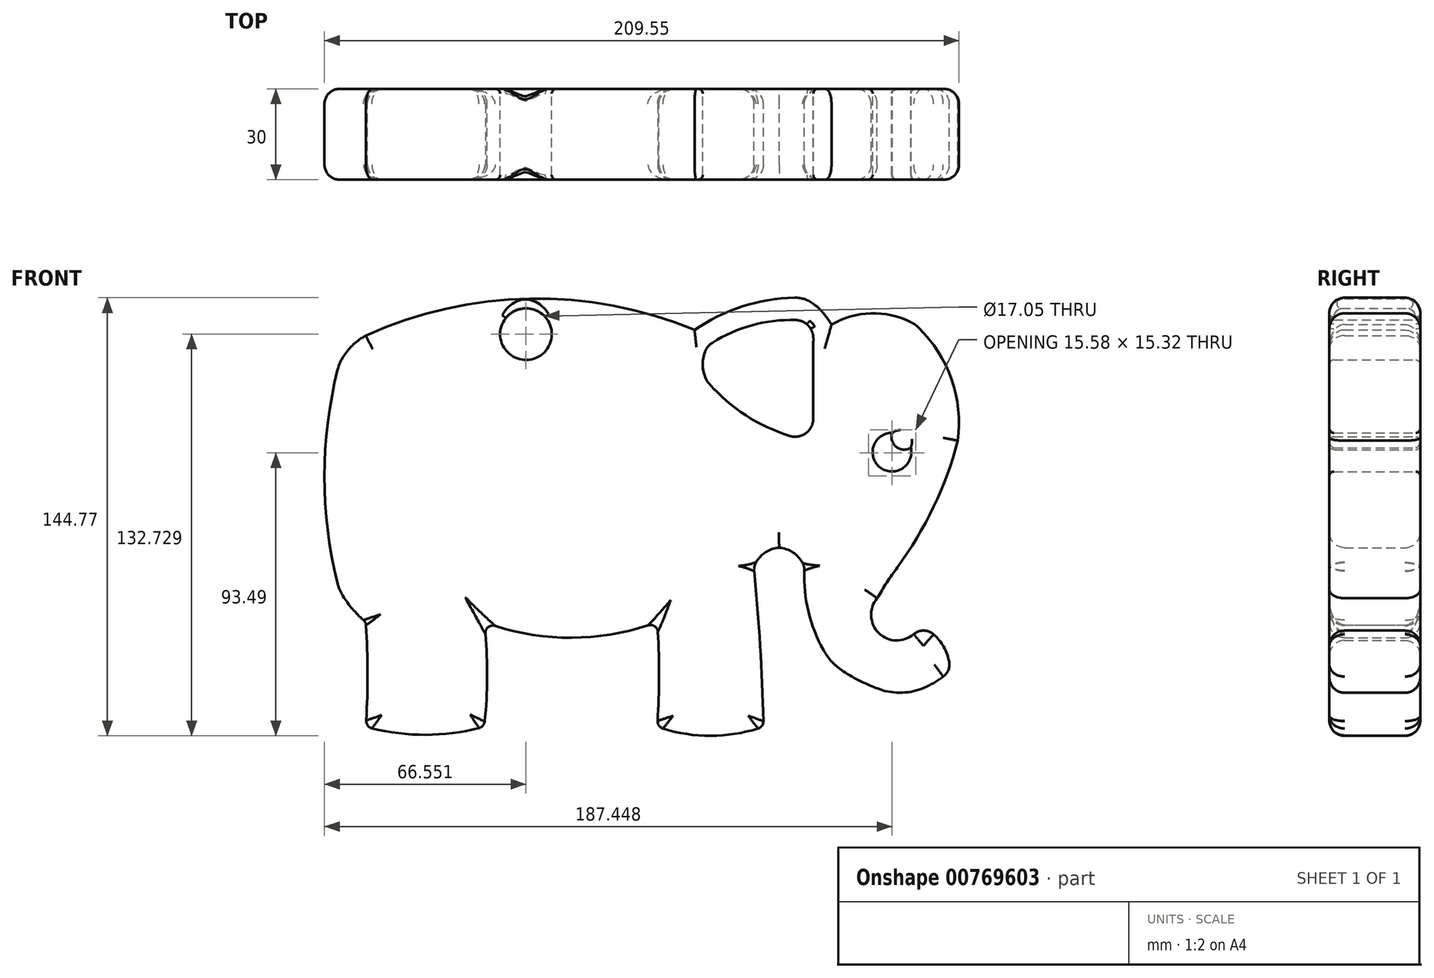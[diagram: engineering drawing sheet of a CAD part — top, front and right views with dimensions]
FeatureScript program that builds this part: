
annotation { "Feature Type Name" : "Feature", "Feature Type Description" : "" }
export const myFeature = defineFeature(function(context is Context, id is Id, definition is map)
    precondition{}
    {
        {
            var Q0;
            Q0=qCreatedBy(makeId("Front.planeOp"),FACE);
            var sketch = newSketch(context, id + "F0", { "sketchPlane" : qUnion([Q0])});
            skArc(sketch, "E0", {"start": v(19.89, -18.97) * mm, "mid": v(21.78, -31.57) * mm, "end": v(34.05, -28.13) * mm});
            skArc(sketch, "E1", {"start": v(27.2, -50.9) * mm, "mid": v(36.15, -48.2) * mm, "end": v(43.95, -43.06) * mm});
            skArc(sketch, "E2", {"start": v(4.8, -40.36) * mm, "mid": v(15.42, -46.87) * mm, "end": v(27.2, -50.9) * mm});
            skArc(sketch, "E3", {"start": v(-4.12, -8.77) * mm, "mid": v(-2.32, -25.31) * mm, "end": v(4.8, -40.36) * mm});
            skArc(sketch, "E4", {"start": v(-4.12, -8.77) * mm, "mid": v(-7.32, -4.26) * mm, "end": v(-12.49, -2.28) * mm});
            skArc(sketch, "E5", {"start": v(-12.49, -2.28) * mm, "mid": v(-17.64, -4.28) * mm, "end": v(-20.86, -8.77) * mm});
            skPoint(sketch, "E6.endSnap0", {"position": v(-17.64, -4.28) * mm});
            skArc(sketch, "E7", {"start": v(-52.73, -61.43) * mm, "mid": v(-35.18, -64.43) * mm, "end": v(-17.64, -61.43) * mm});
            skArc(sketch, "E8", {"start": v(-52.73, -61.43) * mm, "mid": v(-52.15, -44.14) * mm, "end": v(-52.73, -26.86) * mm});
            skArc(sketch, "E9", {"start": v(-109.9, -26.86) * mm, "mid": v(-81.32, -32.04) * mm, "end": v(-52.73, -26.86) * mm});
            skArc(sketch, "E10", {"start": v(-109.9, -61.43) * mm, "mid": v(-108.9, -44.14) * mm, "end": v(-109.9, -26.86) * mm});
            skArc(sketch, "E11", {"start": v(-148.97, -61.43) * mm, "mid": v(-129.44, -64.1) * mm, "end": v(-109.9, -61.43) * mm});
            skArc(sketch, "E12", {"start": v(-148.97, -61.43) * mm, "mid": v(-148.4, -44.14) * mm, "end": v(-148.97, -26.86) * mm});
            skArc(sketch, "E13", {"start": v(-157.82, -15.96) * mm, "mid": v(-153.93, -21.85) * mm, "end": v(-148.97, -26.86) * mm});
            skArc(sketch, "E14", {"start": v(-157.82, 58.3) * mm, "mid": v(-162.64, 21.17) * mm, "end": v(-157.82, -15.96) * mm});
            skArc(sketch, "E15", {"start": v(-148.97, 67.84) * mm, "mid": v(-154.15, 63.77) * mm, "end": v(-157.82, 58.3) * mm});
            skArc(sketch, "E16", {"start": v(-40.42, 69.65) * mm, "mid": v(-94.88, 80.02) * mm, "end": v(-148.97, 67.84) * mm});
            skArc(sketch, "E17", {"start": v(-4.12, 80.33) * mm, "mid": v(-23.12, 77.87) * mm, "end": v(-40.42, 69.65) * mm});
            skArc(sketch, "E18", {"start": v(4.8, 71.47) * mm, "mid": v(0.93, 76.49) * mm, "end": v(-4.12, 80.33) * mm});
            skArc(sketch, "E19", {"start": v(32.47, 71.47) * mm, "mid": v(18.64, 75.18) * mm, "end": v(4.8, 71.47) * mm});
            skArc(sketch, "E20", {"start": v(46.55, 33.1) * mm, "mid": v(44.2, 54) * mm, "end": v(32.47, 71.47) * mm});
            skArc(sketch, "E21", {"start": v(26.57, -8.77) * mm, "mid": v(38.54, 11.22) * mm, "end": v(46.55, 33.1) * mm});
            skArc(sketch, "E22", {"start": v(26.57, -8.77) * mm, "mid": v(23.1, -13.78) * mm, "end": v(19.89, -18.97) * mm});
            skArc(sketch, "E23", {"start": v(-17.64, -61.43) * mm, "mid": v(-18.71, -35.06) * mm, "end": v(-20.86, -8.77) * mm});
            skArc(sketch, "E24", {"start": v(43.95, -43.06) * mm, "mid": v(41.27, -34.1) * mm, "end": v(34.05, -28.13) * mm});
            skArc(sketch, "E25", {"start": v(-1.12, 72.43) * mm, "mid": v(-19.3, 71.76) * mm, "end": v(-35.98, 64.48) * mm});
            skArc(sketch, "E26", {"start": v(-35.98, 64.48) * mm, "mid": v(-37.72, 58.4) * mm, "end": v(-35.98, 52.33) * mm});
            skArc(sketch, "E27", {"start": v(-1.12, 72.43) * mm, "mid": v(-1.26, 52.61) * mm, "end": v(-1.12, 32.8) * mm});
            skArc(sketch, "E28", {"start": v(-35.98, 52.33) * mm, "mid": v(-20.25, 39.52) * mm, "end": v(-1.12, 32.8) * mm});
            skArc(sketch, "E29", {"start": v(24.88, 35.66) * mm, "mid": v(20.77, 24.3) * mm, "end": v(30.98, 30.77) * mm});
            skArc(sketch, "E30", {"start": v(24.88, 35.66) * mm, "mid": v(26.18, 31.04) * mm, "end": v(30.98, 30.77) * mm});
            skCircle(sketch, "E31", {"center": v(-96.09, 68.3) * mm, "radius": 8.53 * mm});
            skSolve(sketch);
        }
        {
            var Q0;
            Q0=makeQuery(id+"F0.imprint","IMPRINT",FACE,{"disambiguationData":[TD([[makeQuery(id+"F0.imprint","IMPRINT",EDGE,{"derivedFrom":sQuery(id+"F0.wireOp",EDGE,"E0")}),-1.0]])]});
            extrude(context, id + "F1", {"entities" : qUnion([Q0]), "depth" : 30 * mm, "offsetDistance" : 25 * mm});
        }
        {
            var Q0;
            Q0=makeQuery(id+"F1.opExtrude","CAP_EDGE",EDGE,{"disambiguationData":[OSD([sQuery(id+"F0.wireOp",EDGE,"E16")])],"isStart":false});
            var Q1;
            Q1=makeQuery(id+"F1.opExtrude","CAP_EDGE",EDGE,{"disambiguationData":[OSD([sQuery(id+"F0.wireOp",EDGE,"E15")])],"isStart":false});
            var Q2;
            Q2=makeQuery(id+"F1.opExtrude","CAP_EDGE",EDGE,{"disambiguationData":[OSD([sQuery(id+"F0.wireOp",EDGE,"E14")])],"isStart":false});
            var Q3;
            Q3=makeQuery(id+"F1.opExtrude","CAP_EDGE",EDGE,{"disambiguationData":[OSD([sQuery(id+"F0.wireOp",EDGE,"E13")])],"isStart":false});
            var Q4;
            Q4=makeQuery(id+"F1.opExtrude","CAP_EDGE",EDGE,{"disambiguationData":[OSD([sQuery(id+"F0.wireOp",EDGE,"E12")])],"isStart":false});
            var Q5;
            Q5=makeQuery(id+"F1.opExtrude","CAP_EDGE",EDGE,{"disambiguationData":[OSD([sQuery(id+"F0.wireOp",EDGE,"E11")])],"isStart":false});
            var Q6;
            Q6=makeQuery(id+"F1.opExtrude","CAP_EDGE",EDGE,{"disambiguationData":[OSD([sQuery(id+"F0.wireOp",EDGE,"E10")])],"isStart":false});
            var Q7;
            Q7=makeQuery(id+"F1.opExtrude","CAP_EDGE",EDGE,{"disambiguationData":[OSD([sQuery(id+"F0.wireOp",EDGE,"E9")])],"isStart":false});
            var Q8;
            Q8=makeQuery(id+"F1.opExtrude","CAP_EDGE",EDGE,{"disambiguationData":[OSD([sQuery(id+"F0.wireOp",EDGE,"E8")])],"isStart":false});
            var Q9;
            Q9=makeQuery(id+"F1.opExtrude","CAP_EDGE",EDGE,{"disambiguationData":[OSD([sQuery(id+"F0.wireOp",EDGE,"E23")])],"isStart":false});
            var Q10;
            Q10=makeQuery(id+"F1.opExtrude","CAP_EDGE",EDGE,{"disambiguationData":[OSD([sQuery(id+"F0.wireOp",EDGE,"E7")])],"isStart":false});
            var Q11;
            Q11=makeQuery(id+"F1.opExtrude","CAP_EDGE",EDGE,{"disambiguationData":[OSD([sQuery(id+"F0.wireOp",EDGE,"E4")])],"isStart":false});
            var Q12;
            Q12=makeQuery(id+"F1.opExtrude","CAP_EDGE",EDGE,{"disambiguationData":[OSD([sQuery(id+"F0.wireOp",EDGE,"E5")])],"isStart":false});
            var Q13;
            Q13=makeQuery(id+"F1.opExtrude","CAP_EDGE",EDGE,{"disambiguationData":[OSD([sQuery(id+"F0.wireOp",EDGE,"E2")])],"isStart":false});
            var Q14;
            Q14=makeQuery(id+"F1.opExtrude","CAP_EDGE",EDGE,{"disambiguationData":[OSD([sQuery(id+"F0.wireOp",EDGE,"E3")])],"isStart":false});
            var Q15;
            Q15=makeQuery(id+"F1.opExtrude","CAP_EDGE",EDGE,{"disambiguationData":[OSD([sQuery(id+"F0.wireOp",EDGE,"E24")])],"isStart":false});
            var Q16;
            Q16=makeQuery(id+"F1.opExtrude","CAP_EDGE",EDGE,{"disambiguationData":[OSD([sQuery(id+"F0.wireOp",EDGE,"E1")])],"isStart":false});
            var Q17;
            Q17=makeQuery(id+"F1.opExtrude","CAP_EDGE",EDGE,{"disambiguationData":[OSD([sQuery(id+"F0.wireOp",EDGE,"E0")])],"isStart":false});
            var Q18;
            Q18=makeQuery(id+"F1.opExtrude","CAP_EDGE",EDGE,{"disambiguationData":[OSD([sQuery(id+"F0.wireOp",EDGE,"E22")])],"isStart":false});
            var Q19;
            Q19=makeQuery(id+"F1.opExtrude","CAP_EDGE",EDGE,{"disambiguationData":[OSD([sQuery(id+"F0.wireOp",EDGE,"E21")])],"isStart":false});
            var Q20;
            Q20=makeQuery(id+"F1.opExtrude","CAP_EDGE",EDGE,{"disambiguationData":[OSD([sQuery(id+"F0.wireOp",EDGE,"E20")])],"isStart":false});
            var Q21;
            Q21=makeQuery(id+"F1.opExtrude","CAP_EDGE",EDGE,{"disambiguationData":[OSD([sQuery(id+"F0.wireOp",EDGE,"E19")])],"isStart":false});
            var Q22;
            Q22=makeQuery(id+"F1.opExtrude","CAP_EDGE",EDGE,{"disambiguationData":[OSD([sQuery(id+"F0.wireOp",EDGE,"E18")])],"isStart":false});
            var Q23;
            Q23=makeQuery(id+"F1.opExtrude","CAP_EDGE",EDGE,{"disambiguationData":[OSD([sQuery(id+"F0.wireOp",EDGE,"E17")])],"isStart":false});
            var Q24;
            Q24=makeQuery(id+"F1.opExtrude","CAP_EDGE",EDGE,{"disambiguationData":[OSD([sQuery(id+"F0.wireOp",EDGE,"E16")])],"isStart":true});
            var Q25;
            Q25=makeQuery(id+"F1.opExtrude","CAP_EDGE",EDGE,{"disambiguationData":[OSD([sQuery(id+"F0.wireOp",EDGE,"E15")])],"isStart":true});
            var Q26;
            Q26=makeQuery(id+"F1.opExtrude","CAP_EDGE",EDGE,{"disambiguationData":[OSD([sQuery(id+"F0.wireOp",EDGE,"E14")])],"isStart":true});
            var Q27;
            Q27=makeQuery(id+"F1.opExtrude","CAP_EDGE",EDGE,{"disambiguationData":[OSD([sQuery(id+"F0.wireOp",EDGE,"E13")])],"isStart":true});
            var Q28;
            Q28=makeQuery(id+"F1.opExtrude","CAP_EDGE",EDGE,{"disambiguationData":[OSD([sQuery(id+"F0.wireOp",EDGE,"E12")])],"isStart":true});
            var Q29;
            Q29=makeQuery(id+"F1.opExtrude","CAP_EDGE",EDGE,{"disambiguationData":[OSD([sQuery(id+"F0.wireOp",EDGE,"E11")])],"isStart":true});
            var Q30;
            Q30=makeQuery(id+"F1.opExtrude","CAP_EDGE",EDGE,{"disambiguationData":[OSD([sQuery(id+"F0.wireOp",EDGE,"E10")])],"isStart":true});
            var Q31;
            Q31=makeQuery(id+"F1.opExtrude","CAP_EDGE",EDGE,{"disambiguationData":[OSD([sQuery(id+"F0.wireOp",EDGE,"E9")])],"isStart":true});
            var Q32;
            Q32=makeQuery(id+"F1.opExtrude","CAP_EDGE",EDGE,{"disambiguationData":[OSD([sQuery(id+"F0.wireOp",EDGE,"E8")])],"isStart":true});
            var Q33;
            Q33=makeQuery(id+"F1.opExtrude","CAP_EDGE",EDGE,{"disambiguationData":[OSD([sQuery(id+"F0.wireOp",EDGE,"E7")])],"isStart":true});
            var Q34;
            Q34=makeQuery(id+"F1.opExtrude","CAP_EDGE",EDGE,{"disambiguationData":[OSD([sQuery(id+"F0.wireOp",EDGE,"E23")])],"isStart":true});
            var Q35;
            Q35=makeQuery(id+"F1.opExtrude","CAP_EDGE",EDGE,{"disambiguationData":[OSD([sQuery(id+"F0.wireOp",EDGE,"E5")])],"isStart":true});
            var Q36;
            Q36=makeQuery(id+"F1.opExtrude","CAP_EDGE",EDGE,{"disambiguationData":[OSD([sQuery(id+"F0.wireOp",EDGE,"E4")])],"isStart":true});
            var Q37;
            Q37=makeQuery(id+"F1.opExtrude","CAP_EDGE",EDGE,{"disambiguationData":[OSD([sQuery(id+"F0.wireOp",EDGE,"E3")])],"isStart":true});
            var Q38;
            Q38=makeQuery(id+"F1.opExtrude","CAP_EDGE",EDGE,{"disambiguationData":[OSD([sQuery(id+"F0.wireOp",EDGE,"E2")])],"isStart":true});
            var Q39;
            Q39=makeQuery(id+"F1.opExtrude","CAP_EDGE",EDGE,{"disambiguationData":[OSD([sQuery(id+"F0.wireOp",EDGE,"E1")])],"isStart":true});
            var Q40;
            Q40=makeQuery(id+"F1.opExtrude","CAP_EDGE",EDGE,{"disambiguationData":[OSD([sQuery(id+"F0.wireOp",EDGE,"E24")])],"isStart":true});
            var Q41;
            Q41=makeQuery(id+"F1.opExtrude","CAP_EDGE",EDGE,{"disambiguationData":[OSD([sQuery(id+"F0.wireOp",EDGE,"E0")])],"isStart":true});
            var Q42;
            Q42=makeQuery(id+"F1.opExtrude","CAP_EDGE",EDGE,{"disambiguationData":[OSD([sQuery(id+"F0.wireOp",EDGE,"E22")])],"isStart":true});
            var Q43;
            Q43=makeQuery(id+"F1.opExtrude","CAP_EDGE",EDGE,{"disambiguationData":[OSD([sQuery(id+"F0.wireOp",EDGE,"E21")])],"isStart":true});
            var Q44;
            Q44=makeQuery(id+"F1.opExtrude","CAP_EDGE",EDGE,{"disambiguationData":[OSD([sQuery(id+"F0.wireOp",EDGE,"E20")])],"isStart":true});
            var Q45;
            Q45=makeQuery(id+"F1.opExtrude","CAP_EDGE",EDGE,{"disambiguationData":[OSD([sQuery(id+"F0.wireOp",EDGE,"E19")])],"isStart":true});
            var Q46;
            Q46=makeQuery(id+"F1.opExtrude","CAP_EDGE",EDGE,{"disambiguationData":[OSD([sQuery(id+"F0.wireOp",EDGE,"E18")])],"isStart":true});
            var Q47;
            Q47=makeQuery(id+"F1.opExtrude","CAP_EDGE",EDGE,{"disambiguationData":[OSD([sQuery(id+"F0.wireOp",EDGE,"E17")])],"isStart":true});
            fillet(context, id + "F2", {"entities" : qUnion([Q0, Q1, Q2, Q3, Q4, Q5, Q6, Q7, Q8, Q9, Q10, Q11, Q12, Q13, Q14, Q15, Q16, Q17, Q18, Q19, Q20, Q21, Q22, Q23, Q24, Q25, Q26, Q27, Q28, Q29, Q30, Q31, Q32, Q33, Q34, Q35, Q36, Q37, Q38, Q39, Q40, Q41, Q42, Q43, Q44, Q45, Q46, Q47]), "radius" : 5 * mm, "tangentPropagation" : true, "allowEdgeOverflow" : false});
        }
        {
            var Q0;
            Q0=makeQuery(id+"F1.opExtrude","SWEPT_EDGE",EDGE,{"disambiguationData":[OSD([sQuery(id+"F0.wireOp",EDGE,"E2"),sQuery(id+"F0.wireOp",EDGE,"E3")])]});
            var Q1;
            Q1=makeQuery(id+"F1.opExtrude","SWEPT_EDGE",EDGE,{"disambiguationData":[OSD([sQuery(id+"F0.wireOp",EDGE,"E1"),sQuery(id+"F0.wireOp",EDGE,"E2")])]});
            fillet(context, id + "F3", {"entities" : qUnion([Q0, Q1]), "radius" : 20 * mm, "tangentPropagation" : true, "allowEdgeOverflow" : false});
        }
        {
            var Q0;
            Q0=makeQuery(id+"F1.opExtrude","SWEPT_EDGE",EDGE,{"disambiguationData":[OSD([sQuery(id+"F0.wireOp",EDGE,"E13"),sQuery(id+"F0.wireOp",EDGE,"E14")])]});
            var Q1;
            Q1=makeQuery(id+"F1.opExtrude","SWEPT_EDGE",EDGE,{"disambiguationData":[OSD([sQuery(id+"F0.wireOp",EDGE,"E14"),sQuery(id+"F0.wireOp",EDGE,"E15")])]});
            fillet(context, id + "F4", {"entities" : qUnion([Q0, Q1]), "radius" : 15 * mm, "tangentPropagation" : true, "allowEdgeOverflow" : false});
        }
        {
            var Q0;
            Q0=makeQuery(id+"F1.opExtrude","SWEPT_EDGE",EDGE,{"disambiguationData":[OSD([sQuery(id+"F0.wireOp",EDGE,"E19"),sQuery(id+"F0.wireOp",EDGE,"E20")])]});
            var Q1;
            Q1=makeQuery(id+"F1.opExtrude","SWEPT_EDGE",EDGE,{"disambiguationData":[OSD([sQuery(id+"F0.wireOp",EDGE,"E17"),sQuery(id+"F0.wireOp",EDGE,"E18")])]});
            fillet(context, id + "F5", {"entities" : qUnion([Q0, Q1]), "radius" : 10 * mm, "tangentPropagation" : true, "allowEdgeOverflow" : false});
        }
        {
            var Q0;
            Q0=makeQuery(id+"F1.opExtrude","SWEPT_EDGE",EDGE,{"disambiguationData":[OSD([sQuery(id+"F0.wireOp",EDGE,"E27"),sQuery(id+"F0.wireOp",EDGE,"E28")])]});
            var Q1;
            Q1=makeQuery(id+"F1.opExtrude","SWEPT_EDGE",EDGE,{"disambiguationData":[OSD([sQuery(id+"F0.wireOp",EDGE,"E25"),sQuery(id+"F0.wireOp",EDGE,"E27")])]});
            var Q2;
            Q2=makeQuery(id+"F1.opExtrude","SWEPT_EDGE",EDGE,{"disambiguationData":[OSD([sQuery(id+"F0.wireOp",EDGE,"E25"),sQuery(id+"F0.wireOp",EDGE,"E26")])]});
            var Q3;
            Q3=makeQuery(id+"F1.opExtrude","SWEPT_EDGE",EDGE,{"disambiguationData":[OSD([sQuery(id+"F0.wireOp",EDGE,"E26"),sQuery(id+"F0.wireOp",EDGE,"E28")])]});
            fillet(context, id + "F6", {"entities" : qUnion([Q0, Q1, Q2, Q3]), "radius" : 6 * mm, "tangentPropagation" : true, "allowEdgeOverflow" : false});
        }
        {
            var Q0;
            Q0=makeQuery(id+"F1.opExtrude","SWEPT_EDGE",EDGE,{"disambiguationData":[OSD([sQuery(id+"F0.wireOp",EDGE,"E1"),sQuery(id+"F0.wireOp",EDGE,"E24")])]});
            var Q1;
            Q1=makeQuery(id+"F1.opExtrude","SWEPT_EDGE",EDGE,{"disambiguationData":[OSD([sQuery(id+"F0.wireOp",EDGE,"E0"),sQuery(id+"F0.wireOp",EDGE,"E24")])]});
            fillet(context, id + "F7", {"entities" : qUnion([Q0, Q1]), "radius" : 5 * mm, "tangentPropagation" : true, "allowEdgeOverflow" : false});
        }
        {
            var Q0;
            Q0=makeQuery(id+"F1.opExtrude","SWEPT_EDGE",EDGE,{"disambiguationData":[OSD([sQuery(id+"F0.wireOp",EDGE,"E10"),sQuery(id+"F0.wireOp",EDGE,"E11")])]});
            var Q1;
            Q1=makeQuery(id+"F1.opExtrude","SWEPT_EDGE",EDGE,{"disambiguationData":[OSD([sQuery(id+"F0.wireOp",EDGE,"E7"),sQuery(id+"F0.wireOp",EDGE,"E8")])]});
            var Q2;
            Q2=makeQuery(id+"F1.opExtrude","SWEPT_EDGE",EDGE,{"disambiguationData":[OSD([sQuery(id+"F0.wireOp",EDGE,"E7"),sQuery(id+"F0.wireOp",EDGE,"E23")])]});
            var Q3;
            Q3=makeQuery(id+"F1.opExtrude","SWEPT_EDGE",EDGE,{"disambiguationData":[OSD([sQuery(id+"F0.wireOp",EDGE,"E11"),sQuery(id+"F0.wireOp",EDGE,"E12")])]});
            var Q4;
            Q4=makeQuery(id+"F1.opExtrude","SWEPT_EDGE",EDGE,{"disambiguationData":[OSD([sQuery(id+"F0.wireOp",EDGE,"E12"),sQuery(id+"F0.wireOp",EDGE,"E13")])]});
            var Q5;
            Q5=makeQuery(id+"F1.opExtrude","SWEPT_EDGE",EDGE,{"disambiguationData":[OSD([sQuery(id+"F0.wireOp",EDGE,"E8"),sQuery(id+"F0.wireOp",EDGE,"E9")])]});
            var Q6;
            Q6=makeQuery(id+"F1.opExtrude","SWEPT_EDGE",EDGE,{"disambiguationData":[OSD([sQuery(id+"F0.wireOp",EDGE,"E9"),sQuery(id+"F0.wireOp",EDGE,"E10")])]});
            fillet(context, id + "F8", {"entities" : qUnion([Q0, Q1, Q2, Q3, Q4, Q5, Q6]), "radius" : 2.5 * mm, "tangentPropagation" : true, "allowEdgeOverflow" : false});
        }
        {
            var Q0;
            Q0=makeQuery(id+"F1.opExtrude","SWEPT_EDGE",EDGE,{"disambiguationData":[OSD([sQuery(id+"F0.wireOp",EDGE,"E5"),sQuery(id+"F0.wireOp",EDGE,"E23")])]});
            var Q1;
            Q1=makeQuery(id+"F1.opExtrude","SWEPT_EDGE",EDGE,{"disambiguationData":[OSD([sQuery(id+"F0.wireOp",EDGE,"E3"),sQuery(id+"F0.wireOp",EDGE,"E4")])]});
            fillet(context, id + "F9", {"entities" : qUnion([Q0, Q1]), "radius" : 5 * mm, "tangentPropagation" : true, "allowEdgeOverflow" : false});
        }
        {
            var Q0;
            Q0=makeQuery(id+"F1.opExtrude","CAP_EDGE",EDGE,{"disambiguationData":[OSD([sQuery(id+"F0.wireOp",EDGE,"E31")])],"isStart":false});
            var Q1;
            Q1=makeQuery(id+"F1.opExtrude","CAP_EDGE",EDGE,{"disambiguationData":[OSD([sQuery(id+"F0.wireOp",EDGE,"E31")])],"isStart":true});
            var Q2;
            Q2=makeQuery(id+"F1.opExtrude","CAP_EDGE",EDGE,{"disambiguationData":[OSD([sQuery(id+"F0.wireOp",EDGE,"E28")])],"isStart":false});
            var Q3;
            Q3=makeQuery(id+"F1.opExtrude","CAP_EDGE",EDGE,{"disambiguationData":[OSD([sQuery(id+"F0.wireOp",EDGE,"E26")])],"isStart":false});
            var Q4;
            Q4=makeQuery(id+"F1.opExtrude","CAP_EDGE",EDGE,{"disambiguationData":[OSD([sQuery(id+"F0.wireOp",EDGE,"E30")])],"isStart":false});
            var Q5;
            Q5=makeQuery(id+"F1.opExtrude","CAP_EDGE",EDGE,{"disambiguationData":[OSD([sQuery(id+"F0.wireOp",EDGE,"E29")])],"isStart":false});
            var Q6;
            Q6=makeQuery(id+"F1.opExtrude","CAP_EDGE",EDGE,{"disambiguationData":[OSD([sQuery(id+"F0.wireOp",EDGE,"E30")])],"isStart":true});
            var Q7;
            Q7=makeQuery(id+"F1.opExtrude","CAP_EDGE",EDGE,{"disambiguationData":[OSD([sQuery(id+"F0.wireOp",EDGE,"E29")])],"isStart":true});
            var Q8;
            Q8=makeQuery(id+"F1.opExtrude","CAP_EDGE",EDGE,{"disambiguationData":[OSD([sQuery(id+"F0.wireOp",EDGE,"E28")])],"isStart":true});
            fillet(context, id + "F10", {"entities" : qUnion([Q0, Q1, Q2, Q3, Q4, Q5, Q6, Q7, Q8]), "radius" : 1.5 * mm, "tangentPropagation" : true, "allowEdgeOverflow" : false});
        }
    });
